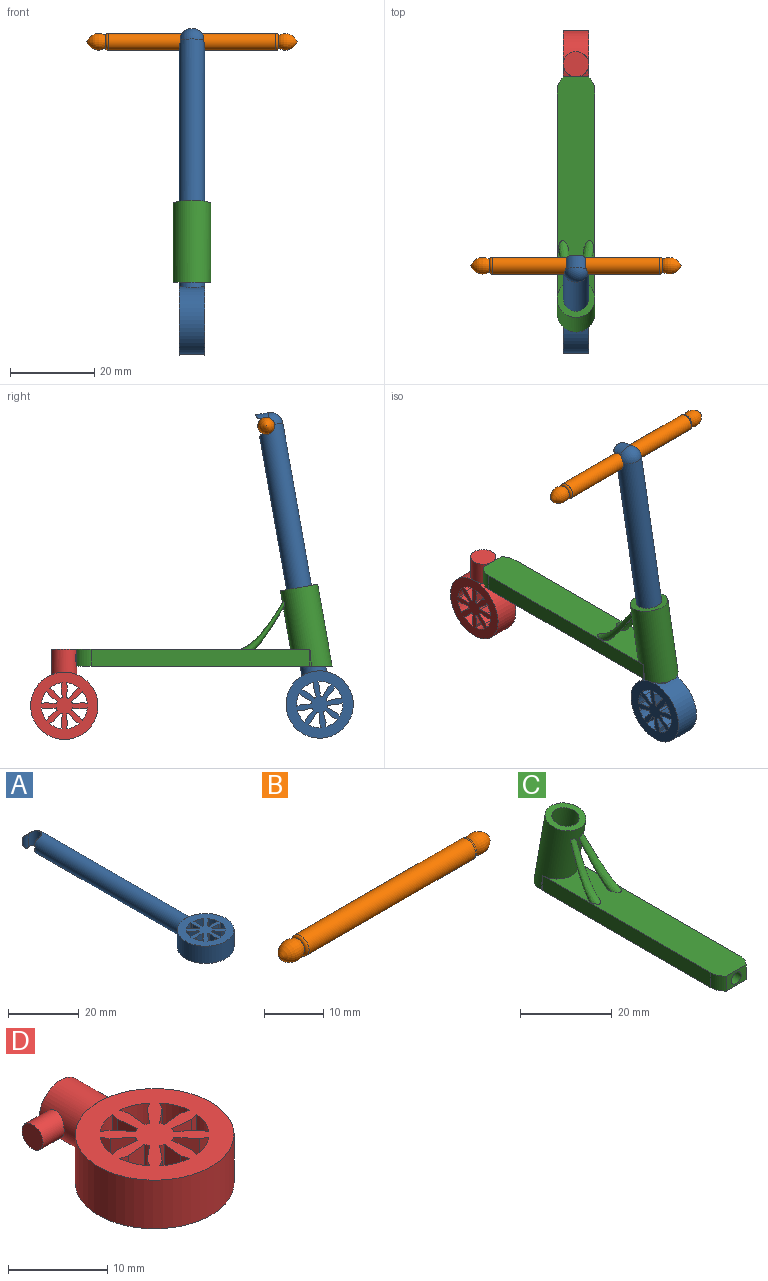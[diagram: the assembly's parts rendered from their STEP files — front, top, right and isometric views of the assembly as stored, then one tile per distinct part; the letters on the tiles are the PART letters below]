
ASSEMBLY  parts=4 mates=3
PART A: 57 faces, bbox 16x78.4x6 mm
  f0: cylinder r=3mm len=60mm, axis (0,-1,0), area 1104.5mm2, adj f1,f51,f55,f56
  f1: sphere r=3mm, area 25.7mm2, adj f0,f2,f56
  f2: cylinder r=3mm len=4.9mm, axis (1,0,0), area 15.1mm2, adj f1,f54,f56
  f3: plane 6x0.87mm, normal (0.86,-0.51,0), area 6.1mm2, adj f4,f43,f52,f53
  f4: cylinder r=5.5mm len=6mm, axis (0,0,-1), area 19.9mm2, adj f3,f5,f52,f53
  f5: plane 6x0.98mm, normal (0.25,0.97,0), area 6.1mm2, adj f4,f6,f52,f53
  f6: plane 6x2.56mm, normal (-0.1,1,0), area 15.5mm2, adj f5,f7,f52,f53
  f7: cylinder r=2mm len=6mm, axis (0,0,-1), area 3.4mm2, adj f6,f43,f52,f53
  f8: cylinder r=5.5mm len=6mm, axis (0,0,-1), area 19.9mm2, adj f9,f44,f52,f53
  f9: plane 6x0.87mm, normal (-0.51,0.86,0), area 6.1mm2, adj f8,f10,f52,f53
  f10: plane 6x1.99mm, normal (-0.77,0.64,0), area 15.5mm2, adj f9,f11,f52,f53
  f11: cylinder r=2mm len=6mm, axis (0,0,-1), area 3.4mm2, adj f10,f12,f52,f53
  f12: plane 6x2.56mm, normal (1,-0.1,0), area 15.5mm2, adj f11,f44,f52,f53
  f13: cylinder r=5.5mm len=6mm, axis (0,0,-1), area 19.9mm2, adj f14,f45,f52,f53
  f14: plane 6x0.98mm, normal (-0.97,0.25,0), area 6.1mm2, adj f13,f15,f52,f53
  f15: plane 6x2.56mm, normal (-1,-0.1,0), area 15.5mm2, adj f14,f16,f52,f53
  f16: cylinder r=2mm len=6mm, axis (0,0,-1), area 3.4mm2, adj f15,f17,f52,f53
  f17: plane 6x1.99mm, normal (0.77,0.64,0), area 15.5mm2, adj f16,f45,f52,f53
  f18: cylinder r=5.5mm len=6mm, axis (0,0,-1), area 19.9mm2, adj f19,f46,f52,f53
  f19: plane 6x0.87mm, normal (-0.86,-0.51,0), area 6.1mm2, adj f18,f20,f52,f53
  f20: plane 6x1.99mm, normal (-0.64,-0.77,0), area 15.5mm2, adj f19,f21,f52,f53
  f21: cylinder r=2mm len=6mm, axis (0,0,-1), area 3.4mm2, adj f20,f22,f52,f53
  f22: plane 6x2.56mm, normal (0.1,1,0), area 15.5mm2, adj f21,f46,f52,f53
  f23: cylinder r=5.5mm len=6mm, axis (0,0,-1), area 19.9mm2, adj f24,f47,f52,f53
  f24: plane 6x0.98mm, normal (-0.25,-0.97,0), area 6.1mm2, adj f23,f25,f52,f53
  f25: plane 6x2.56mm, normal (0.1,-1,0), area 15.5mm2, adj f24,f26,f52,f53
  f26: cylinder r=2mm len=6mm, axis (0,0,-1), area 3.4mm2, adj f25,f27,f52,f53
  f27: plane 6x1.99mm, normal (-0.64,0.77,0), area 15.5mm2, adj f26,f47,f52,f53
  f28: cylinder r=5.5mm len=6mm, axis (0,0,-1), area 19.9mm2, adj f29,f48,f52,f53
  f29: plane 6x0.87mm, normal (0.51,-0.86,0), area 6.1mm2, adj f28,f30,f52,f53
  f30: plane 6x1.99mm, normal (0.77,-0.64,0), area 15.5mm2, adj f29,f31,f52,f53
  f31: cylinder r=2mm len=6mm, axis (0,0,-1), area 3.4mm2, adj f30,f32,f52,f53
  f32: plane 6x2.56mm, normal (-1,0.1,0), area 15.5mm2, adj f31,f48,f52,f53
  f33: cylinder r=5.5mm len=6mm, axis (0,0,-1), area 19.9mm2, adj f34,f49,f52,f53
  f34: plane 6x0.98mm, normal (0.97,-0.25,0), area 6.1mm2, adj f33,f35,f52,f53
  f35: plane 6x2.56mm, normal (1,0.1,0), area 15.5mm2, adj f34,f36,f52,f53
  f36: cylinder r=2mm len=6mm, axis (0,0,-1), area 3.4mm2, adj f35,f37,f52,f53
  f37: plane 6x1.99mm, normal (-0.77,-0.64,0), area 15.5mm2, adj f36,f49,f52,f53
  f38: cylinder r=5.5mm len=6mm, axis (0,0,-1), area 19.9mm2, adj f39,f50,f52,f53
  f39: plane 6x0.87mm, normal (0.86,0.51,0), area 6.1mm2, adj f38,f40,f52,f53
  f40: plane 6x1.99mm, normal (0.64,0.77,0), area 15.5mm2, adj f39,f41,f52,f53
  f41: cylinder r=2mm len=6mm, axis (0,0,-1), area 3.4mm2, adj f40,f42,f52,f53
  f42: plane 6x2.56mm, normal (-0.1,-1,0), area 15.5mm2, adj f41,f50,f52,f53
  f43: plane 6x1.99mm, normal (0.64,-0.77,0), area 15.5mm2, adj f3,f7,f52,f53
  f44: plane 6x0.98mm, normal (0.97,0.25,0), area 6.1mm2, adj f8,f12,f52,f53
  f45: plane 6x0.87mm, normal (0.51,0.86,0), area 6.1mm2, adj f13,f17,f52,f53
  f46: plane 6x0.98mm, normal (-0.25,0.97,0), area 6.1mm2, adj f18,f22,f52,f53
  f47: plane 6x0.87mm, normal (-0.86,0.51,0), area 6.1mm2, adj f23,f27,f52,f53
  f48: plane 6x0.98mm, normal (-0.97,-0.25,0), area 6.1mm2, adj f28,f32,f52,f53
  f49: plane 6x0.87mm, normal (-0.51,-0.86,0), area 6.1mm2, adj f33,f37,f52,f53
  f50: plane 6x0.98mm, normal (0.25,-0.97,0), area 6.1mm2, adj f38,f42,f52,f53
  f51: cylinder r=8mm len=16mm, axis (0,0,-1), area 272.8mm2, adj f0,f52,f53
  f52: plane 16x16mm, normal (0,0,1), area 153.8mm2, adj f3,f4,f5,f6,f7,f8,f9,f10
  f53: plane 16x16mm, normal (0,0,-1), area 153.8mm2, adj f3,f4,f5,f6,f7,f8,f9,f10
  f54: cylinder r=1.12mm len=4.68mm, axis (0,0,-1), area 8mm2, adj f2,f56
  f55: cylinder r=0.78mm len=4.68mm, axis (0,0,-1), area 4.3mm2, adj f0,f56
  f56: cylinder r=2mm len=6mm, axis (0,0,-1), area 41.8mm2, adj f0,f1,f2,f54,f55
PART B: 5 faces, bbox 45.5x4.3x4.3 mm
  f0: torus R=1.46mm, axis (1,0,0), area 9.7mm2, adj f1
  f1: cylinder r=2mm len=39.92mm, axis (1,0,0), area 501.6mm2, adj f0,f2
  f2: torus R=1.46mm, axis (1,0,0), area 9.7mm2, adj f1,f3
  f3: revolved ~4.5x3.96mm, area 49.9mm2, adj f2
  f4: revolved ~2.9x1.45mm, area 0mm2
PART C: 16 faces, bbox 9x60.6x21 mm
  f0: cylinder r=3mm len=20.26mm, axis (0,0.17,-0.98), area 357.9mm2, adj f9,f11
  f1: cylinder r=4.5mm len=21.04mm, axis (0,0.17,-0.98), area 477.7mm2, adj f2,f3,f9,f10,f11,f12,f13
  f2: cylinder r=4.5mm len=4mm, axis (0,0,1), area 0.7mm2, adj f1,f4,f9
  f3: cylinder r=4.5mm len=4mm, axis (0,0,1), area 0.7mm2, adj f1,f8,f9
  f4: plane 52x4mm, normal (-1,0,0), area 208mm2, adj f2,f5,f9,f10
  f5: cylinder r=4.5mm len=4mm, axis (0,0,1), area 15.1mm2, adj f4,f6,f9,f10
  f6: plane 6x4mm, normal (0,-1,0), area 16.9mm2, adj f5,f7,f9,f10,f14
  f7: cylinder r=4.5mm len=4mm, axis (0,0,1), area 15.1mm2, adj f6,f8,f9,f10
  f8: plane 52x4mm, normal (1,0,0), area 208mm2, adj f3,f7,f9,f10
  f9: plane 60.63x9mm, normal (0,0,-1), area 505mm2, adj f0,f1,f2,f3,f4,f5,f6,f7
  f10: plane 55.35x9mm, normal (0,0,1), area 450.2mm2, adj f1,f4,f5,f6,f7,f8,f12,f13
  f11: plane 9x8.86mm, normal (0,-0.17,0.98), area 35.3mm2, adj f0,f1
  f12: bspline ~14.34x10.45mm, area 71.2mm2, adj f1,f10
  f13: bspline ~14.34x10.45mm, area 71.2mm2, adj f1,f10
  f14: cylinder r=1.5mm len=3mm, axis (0,-1,0), area 28.3mm2, adj f6,f15
  f15: plane 3x3mm, normal (0,-1,0), area 7.1mm2, adj f14
PART D: 55 faces, bbox 16x21.4x6 mm
  f0: plane 6x0.87mm, normal (0.86,-0.51,0), area 6.1mm2, adj f1,f40,f49,f50
  f1: cylinder r=5.5mm len=6mm, axis (0,0,-1), area 19.9mm2, adj f0,f2,f49,f50
  f2: plane 6x0.98mm, normal (0.25,0.97,0), area 6.1mm2, adj f1,f3,f49,f50
  f3: plane 6x2.56mm, normal (-0.1,1,0), area 15.5mm2, adj f2,f4,f49,f50
  f4: cylinder r=2mm len=6mm, axis (0,0,-1), area 3.4mm2, adj f3,f40,f49,f50
  f5: cylinder r=5.5mm len=6mm, axis (0,0,-1), area 19.9mm2, adj f6,f41,f49,f50
  f6: plane 6x0.87mm, normal (-0.51,0.86,0), area 6.1mm2, adj f5,f7,f49,f50
  f7: plane 6x1.99mm, normal (-0.77,0.64,0), area 15.5mm2, adj f6,f8,f49,f50
  f8: cylinder r=2mm len=6mm, axis (0,0,-1), area 3.4mm2, adj f7,f9,f49,f50
  f9: plane 6x2.56mm, normal (1,-0.1,0), area 15.5mm2, adj f8,f41,f49,f50
  f10: cylinder r=5.5mm len=6mm, axis (0,0,-1), area 19.9mm2, adj f11,f42,f49,f50
  f11: plane 6x0.98mm, normal (-0.97,0.25,0), area 6.1mm2, adj f10,f12,f49,f50
  f12: plane 6x2.56mm, normal (-1,-0.1,0), area 15.5mm2, adj f11,f13,f49,f50
  f13: cylinder r=2mm len=6mm, axis (0,0,-1), area 3.4mm2, adj f12,f14,f49,f50
  f14: plane 6x1.99mm, normal (0.77,0.64,0), area 15.5mm2, adj f13,f42,f49,f50
  f15: cylinder r=5.5mm len=6mm, axis (0,0,-1), area 19.9mm2, adj f16,f43,f49,f50
  f16: plane 6x0.87mm, normal (-0.86,-0.51,0), area 6.1mm2, adj f15,f17,f49,f50
  f17: plane 6x1.99mm, normal (-0.64,-0.77,0), area 15.5mm2, adj f16,f18,f49,f50
  f18: cylinder r=2mm len=6mm, axis (0,0,-1), area 3.4mm2, adj f17,f19,f49,f50
  f19: plane 6x2.56mm, normal (0.1,1,0), area 15.5mm2, adj f18,f43,f49,f50
  f20: cylinder r=5.5mm len=6mm, axis (0,0,-1), area 19.9mm2, adj f21,f44,f49,f50
  f21: plane 6x0.98mm, normal (-0.25,-0.97,0), area 6.1mm2, adj f20,f22,f49,f50
  f22: plane 6x2.56mm, normal (0.1,-1,0), area 15.5mm2, adj f21,f23,f49,f50
  f23: cylinder r=2mm len=6mm, axis (0,0,-1), area 3.4mm2, adj f22,f24,f49,f50
  f24: plane 6x1.99mm, normal (-0.64,0.77,0), area 15.5mm2, adj f23,f44,f49,f50
  f25: cylinder r=5.5mm len=6mm, axis (0,0,-1), area 19.9mm2, adj f26,f45,f49,f50
  f26: plane 6x0.87mm, normal (0.51,-0.86,0), area 6.1mm2, adj f25,f27,f49,f50
  f27: plane 6x1.99mm, normal (0.77,-0.64,0), area 15.5mm2, adj f26,f28,f49,f50
  f28: cylinder r=2mm len=6mm, axis (0,0,-1), area 3.4mm2, adj f27,f29,f49,f50
  f29: plane 6x2.56mm, normal (-1,0.1,0), area 15.5mm2, adj f28,f45,f49,f50
  f30: cylinder r=5.5mm len=6mm, axis (0,0,-1), area 19.9mm2, adj f31,f46,f49,f50
  f31: plane 6x0.98mm, normal (0.97,-0.25,0), area 6.1mm2, adj f30,f32,f49,f50
  f32: plane 6x2.56mm, normal (1,0.1,0), area 15.5mm2, adj f31,f33,f49,f50
  f33: cylinder r=2mm len=6mm, axis (0,0,-1), area 3.4mm2, adj f32,f34,f49,f50
  f34: plane 6x1.99mm, normal (-0.77,-0.64,0), area 15.5mm2, adj f33,f46,f49,f50
  f35: cylinder r=5.5mm len=6mm, axis (0,0,-1), area 19.9mm2, adj f36,f47,f49,f50
  f36: plane 6x0.87mm, normal (0.86,0.51,0), area 6.1mm2, adj f35,f37,f49,f50
  f37: plane 6x1.99mm, normal (0.64,0.77,0), area 15.5mm2, adj f36,f38,f49,f50
  f38: cylinder r=2mm len=6mm, axis (0,0,-1), area 3.4mm2, adj f37,f39,f49,f50
  f39: plane 6x2.56mm, normal (-0.1,-1,0), area 15.5mm2, adj f38,f47,f49,f50
  f40: plane 6x1.99mm, normal (0.64,-0.77,0), area 15.5mm2, adj f0,f4,f49,f50
  f41: plane 6x0.98mm, normal (0.97,0.25,0), area 6.1mm2, adj f5,f9,f49,f50
  f42: plane 6x0.87mm, normal (0.51,0.86,0), area 6.1mm2, adj f10,f14,f49,f50
  f43: plane 6x0.98mm, normal (-0.25,0.97,0), area 6.1mm2, adj f15,f19,f49,f50
  f44: plane 6x0.87mm, normal (-0.86,0.51,0), area 6.1mm2, adj f20,f24,f49,f50
  f45: plane 6x0.98mm, normal (-0.97,-0.25,0), area 6.1mm2, adj f25,f29,f49,f50
  f46: plane 6x0.87mm, normal (-0.51,-0.86,0), area 6.1mm2, adj f30,f34,f49,f50
  f47: plane 6x0.98mm, normal (0.25,-0.97,0), area 6.1mm2, adj f35,f39,f49,f50
  f48: cylinder r=8mm len=16mm, axis (0,0,-1), area 272.8mm2, adj f49,f50,f51
  f49: plane 16x16mm, normal (0,0,1), area 153.8mm2, adj f0,f1,f2,f3,f4,f5,f6,f7
  f50: plane 16x16mm, normal (0,0,-1), area 153.8mm2, adj f0,f1,f2,f3,f4,f5,f6,f7
  f51: cylinder r=3mm len=6mm, axis (0,-1,0), area 100.2mm2, adj f48,f52,f53
  f52: plane 6x6mm, normal (0,1,0), area 28.3mm2, adj f51
  f53: cylinder r=1.5mm len=3.4mm, axis (1,0,0), area 30.1mm2, adj f51,f54
  f54: plane 3x3mm, normal (-1,0,0), area 7.1mm2, adj f53
PLACE A rot(axis=(0.54,-0.64,-0.54),114.4deg) t=(3,-27.86,-1.8)mm
PLACE B rot(axis=(1,0,0),80deg) t=(0,-16.45,57.11)mm
PLACE C rot(axis=(0,0,1),180deg) t=(0,3.17,4)mm
PLACE D rot(axis=(0.58,0.58,0.58),120deg) t=(-3,31.52,-2)mm
MATE fastened C.f0 <-> A.f0  axis (0,-0.17,-0.98) through (0,-24.24,18.7)mm
MATE fastened C.f14 <-> D.f53  axis (0,1,0) through (0,25.52,2)mm
MATE fastened A.f56 <-> B.f1  axis (1,0,0) through (0,-16.45,57.11)mm
